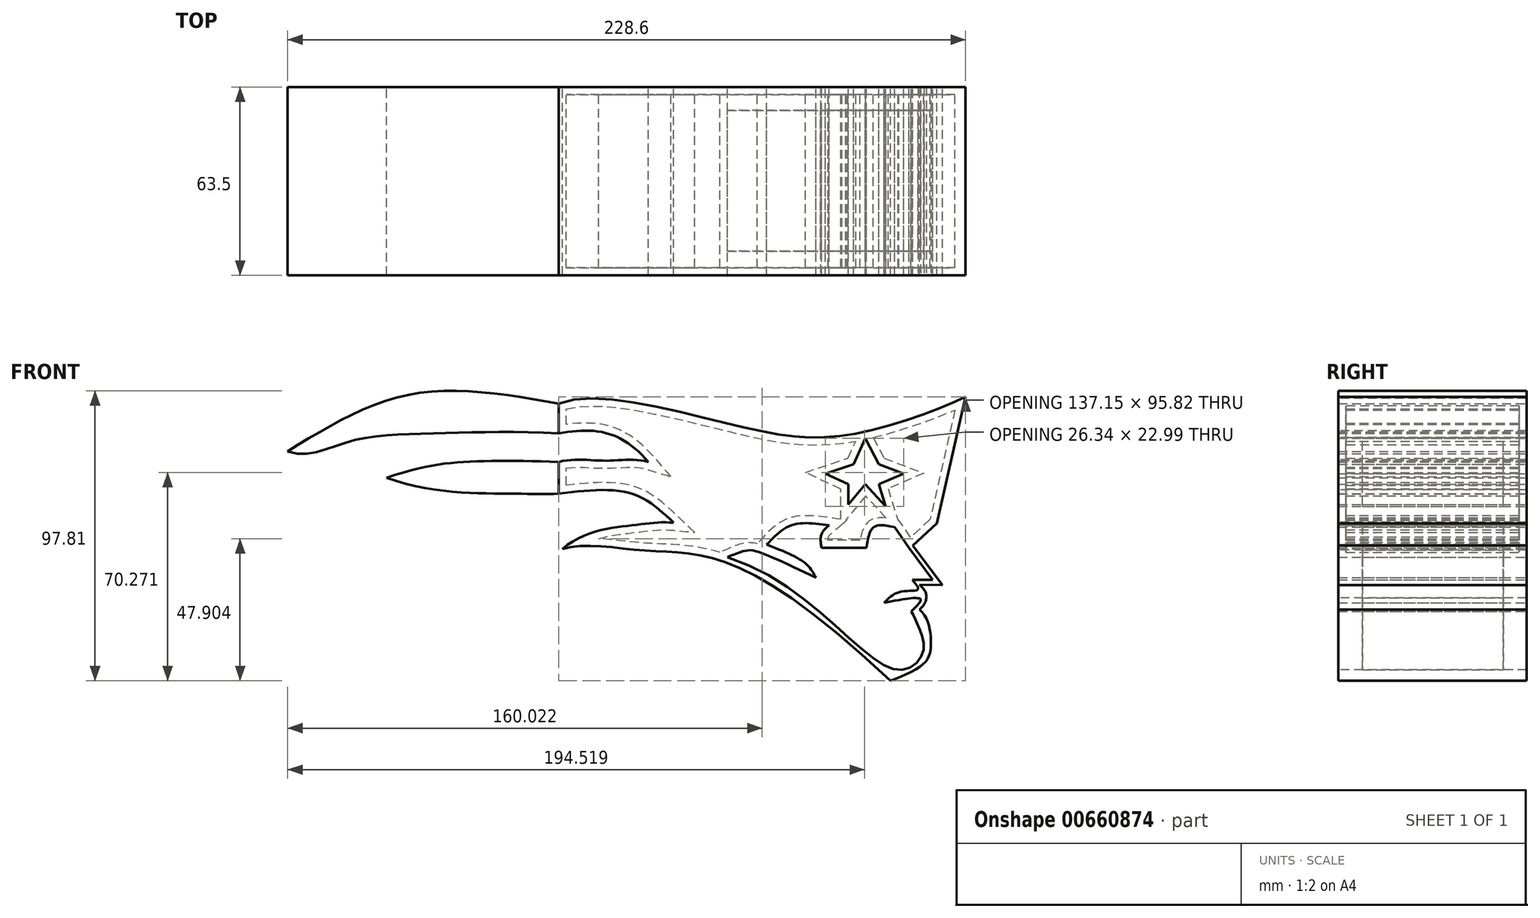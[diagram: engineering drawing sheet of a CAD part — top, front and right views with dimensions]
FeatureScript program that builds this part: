
annotation { "Feature Type Name" : "Feature", "Feature Type Description" : "" }
export const myFeature = defineFeature(function(context is Context, id is Id, definition is map)
    precondition{}
    {
        {
            var Q0;
            Q0=qCreatedBy(makeId("Front.planeOp"),FACE);
            var sketch = newSketch(context, id + "F0", { "sketchPlane" : qUnion([Q0])});
            skFitSpline(sketch, "E0", {"points": [v(-76.55, 30.41) * mm, v(-14.84, 22.52) * mm, v(22.56, 20.11) * mm, v(60.6, 32.7) * mm], "startDerivative": vector(105.9, 41.24) * mm, "endDerivative": vector(88.2, 42.73) * mm});
            skLineSegment(sketch, "E1", {"start": v(60.6, 32.7) * mm, "end": v(50.93, -9.95) * mm});
            skLineSegment(sketch, "E2", {"start": v(50.93, -9.95) * mm, "end": v(42.8, -17.48) * mm});
            skLineSegment(sketch, "E3", {"start": v(42.8, -17.48) * mm, "end": v(52.74, -30.8) * mm});
            skLineSegment(sketch, "E4", {"start": v(52.74, -30.8) * mm, "end": v(45.1, -30.75) * mm});
            skFitSpline(sketch, "E5", {"points": [v(45.1, -39.14) * mm, v(48.83, -51.49) * mm, v(35.22, -63.12) * mm], "startDerivative": vector(21.41, -17.74) * mm, "endDerivative": vector(-66.1, -25.1) * mm});
            skFitSpline(sketch, "E6", {"points": [v(35.22, -63.12) * mm, v(-46.74, -19.26) * mm, v(-75.4, -18.63) * mm], "startDerivative": vector(-230.88, 217.03) * mm, "endDerivative": vector(-62.71, -20.1) * mm});
            skFitSpline(sketch, "E7", {"points": [v(-75.4, -18.63) * mm, v(-51.4, -10.6) * mm, v(-37.88, -9.8) * mm], "startDerivative": vector(40.06, 33.3) * mm, "endDerivative": vector(31.5, -3.1) * mm});
            skFitSpline(sketch, "E8", {"points": [v(-37.88, -9.8) * mm, v(-51.92, 0) * mm, v(-76.55, 0) * mm], "startDerivative": vector(-27.63, 26.46) * mm, "endDerivative": vector(-49.07, -5.88) * mm});
            skLineSegment(sketch, "E9", {"start": v(-76.55, 0) * mm, "end": v(-76.55, 10.68) * mm});
            skFitSpline(sketch, "E10", {"points": [v(-76.55, 10.68) * mm, v(-60.93, 11.13) * mm, v(-46.36, 10.68) * mm], "startDerivative": vector(31.02, 8.7) * mm, "endDerivative": vector(29.37, -8.8) * mm});
            skFitSpline(sketch, "E11", {"points": [v(-46.36, 10.68) * mm, v(-60.4, 20.4) * mm, v(-76.55, 20.4) * mm], "startDerivative": vector(-25.48, 29.64) * mm, "endDerivative": vector(-35.03, -5.68) * mm});
            skLineSegment(sketch, "E12", {"start": v(-76.55, 20.4) * mm, "end": v(-76.55, 30.41) * mm});
            skFitSpline(sketch, "E13", {"points": [v(45.1, -30.75) * mm, v(47.36, -34.55) * mm, v(45.1, -39.14) * mm], "startDerivative": vector(9.64, -8.77) * mm, "endDerivative": vector(-9.59, -9.18) * mm});
            skLineSegment(sketch, "E14", {"start": v(22.81, 9.94) * mm, "end": v(26.74, 18.65) * mm});
            skLineSegment(sketch, "E15", {"start": v(26.74, 18.65) * mm, "end": v(31.35, 9.94) * mm});
            skLineSegment(sketch, "E16", {"start": v(31.35, 9.94) * mm, "end": v(39.69, 6.75) * mm});
            skLineSegment(sketch, "E17", {"start": v(39.69, 6.75) * mm, "end": v(31.35, 3.15) * mm});
            skLineSegment(sketch, "E18", {"start": v(31.35, 3.15) * mm, "end": v(33.67, -4.34) * mm});
            skLineSegment(sketch, "E19", {"start": v(33.67, -4.34) * mm, "end": v(26.74, 3.15) * mm});
            skLineSegment(sketch, "E20", {"start": v(26.74, 3.15) * mm, "end": v(21.08, -3.72) * mm});
            skLineSegment(sketch, "E21", {"start": v(21.08, -3.72) * mm, "end": v(21.08, 3.15) * mm});
            skLineSegment(sketch, "E22", {"start": v(21.08, 3.15) * mm, "end": v(13.35, 6.75) * mm});
            skLineSegment(sketch, "E23", {"start": v(13.35, 6.75) * mm, "end": v(22.81, 9.94) * mm});
            skFitSpline(sketch, "E24", {"points": [v(-19.72, -21.46) * mm, v(37.16, -59.31) * mm, v(46.35, -53) * mm, v(44.17, -43.7) * mm, v(42.26, -39.7) * mm], "startDerivative": vector(172.05, -53.12) * mm, "endDerivative": vector(-18.1, 19.47) * mm});
            skFitSpline(sketch, "E25", {"points": [v(42.26, -39.7) * mm, v(45.37, -35.66) * mm, v(33.17, -36.79) * mm], "startDerivative": vector(13.42, 12.7) * mm, "endDerivative": vector(-28.57, -5.56) * mm});
            skFitSpline(sketch, "E26", {"points": [v(33.17, -36.79) * mm, v(38.55, -33.1) * mm, v(44.46, -32.3) * mm, v(42.61, -29.06) * mm], "startDerivative": vector(12.2, 12.85) * mm, "endDerivative": vector(-12.3, 14.26) * mm});
            skLineSegment(sketch, "E27", {"start": v(42.61, -29.06) * mm, "end": v(49.56, -29.06) * mm});
            skLineSegment(sketch, "E28", {"start": v(49.56, -29.06) * mm, "end": v(41.46, -18.3) * mm});
            skLineSegment(sketch, "E29", {"start": v(41.46, -18.3) * mm, "end": v(36.6, -11.3) * mm});
            skFitSpline(sketch, "E30", {"points": [v(36.6, -11.3) * mm, v(29.63, -11.3) * mm, v(27.15, -18.3) * mm], "startDerivative": vector(-16.46, 3.4) * mm, "endDerivative": vector(-2.53, -17.3) * mm});
            skLineSegment(sketch, "E31", {"start": v(27.15, -18.3) * mm, "end": v(17.15, -18.3) * mm});
            skLineSegment(sketch, "E32", {"start": v(17.15, -18.3) * mm, "end": v(11.98, -18.3) * mm});
            skFitSpline(sketch, "E33", {"points": [v(11.98, -18.3) * mm, v(11.98, -13.65) * mm, v(14.56, -10.67) * mm], "startDerivative": vector(-1.4, 9.63) * mm, "endDerivative": vector(6.67, 5.57) * mm});
            skFitSpline(sketch, "E34", {"points": [v(14.56, -10.67) * mm, v(1.83, -10.67) * mm, v(-6.47, -17.19) * mm], "startDerivative": vector(-26.12, 3.58) * mm, "endDerivative": vector(-15.77, -16.93) * mm});
            skFitSpline(sketch, "E35", {"points": [v(-6.47, -17.19) * mm, v(6.53, -23.48) * mm, v(10.11, -28.33) * mm], "startDerivative": vector(25.14, -9.75) * mm, "endDerivative": vector(6.71, -12.76) * mm});
            skFitSpline(sketch, "E36", {"points": [v(10.11, -28.33) * mm, v(-8.13, -20.05) * mm, v(-13.26, -19.16) * mm, v(-19.72, -21.46) * mm], "startDerivative": vector(-44.29, 21.12) * mm, "endDerivative": vector(-24.53, -10.88) * mm});
            skPoint(sketch, "E37.2.internal.snap0", {"position": v(-76.55, 5.34) * mm});
            skFitSpline(sketch, "E37", {"points": [v(-76.55, 10.68) * mm, v(-108.96, 10.68) * mm, v(-134.69, 5.34) * mm], "startDerivative": vector(-72.18, 2.86) * mm, "endDerivative": vector(-71.3, -24.14) * mm});
            skFitSpline(sketch, "E38", {"points": [v(-134.69, 5.34) * mm, v(-93.5, 0) * mm, v(-76.55, 0) * mm], "startDerivative": vector(74.49, -26.26) * mm, "endDerivative": vector(38.7, 1.31) * mm});
            skFitSpline(sketch, "E39", {"points": [v(-76.55, 30.41) * mm, v(-126.5, 33.5) * mm, v(-168, 14.28) * mm], "startDerivative": vector(-100.97, 17.64) * mm, "endDerivative": vector(-81.78, -50.43) * mm});
            skFitSpline(sketch, "E40", {"points": [v(-168, 14.28) * mm, v(-146.96, 17.64) * mm, v(-119.9, 20.32) * mm, v(-76.55, 20.4) * mm], "startDerivative": vector(73.22, -27.17) * mm, "endDerivative": vector(121.44, -6.34) * mm});
            skSolve(sketch);
        }
        {
            var Q0;
            Q0=makeQuery(id+"F0.imprint","IMPRINT",FACE,{"disambiguationData":[TD([[makeQuery(id+"F0.imprint","IMPRINT",EDGE,{"derivedFrom":sQuery(id+"F0.wireOp",EDGE,"E0")}),-1.0]])]});
            extrude(context, id + "F1", {"entities" : qUnion([Q0]), "depth" : 63.5 * mm, "offsetDistance" : 25.4 * mm});
        }
        {
            var Q0;
            Q0=makeQuery(id+"F0.imprint","IMPRINT",FACE,{"disambiguationData":[TD([[makeQuery(id+"F0.imprint","IMPRINT",EDGE,{"derivedFrom":sQuery(id+"F0.wireOp",EDGE,"E12")}),1.0]])]});
            var Q1;
            Q1=makeQuery(id+"F0.imprint","IMPRINT",FACE,{"disambiguationData":[TD([[makeQuery(id+"F0.imprint","IMPRINT",EDGE,{"derivedFrom":sQuery(id+"F0.wireOp",EDGE,"E9")}),1.0]])]});
            extrude(context, id + "F2", {"entities" : qUnion([Q0, Q1]), "depth" : 63.5 * mm, "offsetDistance" : 25.4 * mm});
        }
        {
            var Q0;
            Q0=makeQuery(id+"F0.imprint","IMPRINT",FACE,{"disambiguationData":[TD([[makeQuery(id+"F0.imprint","IMPRINT",EDGE,{"derivedFrom":sQuery(id+"F0.wireOp",EDGE,"E24")}),1.0]])]});
            var Q1;
            Q1=makeQuery(id+"F0.imprint","IMPRINT",FACE,{"disambiguationData":[TD([[makeQuery(id+"F0.imprint","IMPRINT",EDGE,{"derivedFrom":sQuery(id+"F0.wireOp",EDGE,"E14")}),-1.0]])]});
            extrude(context, id + "F3", {"entities" : qUnion([Q0, Q1]), "depth" : 55.37 * mm, "offsetDistance" : 25.4 * mm, "hasSecondDirection" : true, "secondDirectionOppositeDirection" : false, "secondDirectionDepth" : 7.82 * mm});
        }
        {
            var Q0;
            Q0=makeQuery(id+"F1.opExtrude","CAP_FACE",FACE,{"disambiguationData":[OSD([sQuery(id+"F0.wireOp",EDGE,"E0"),sQuery(id+"F0.wireOp",EDGE,"E1"),sQuery(id+"F0.wireOp",EDGE,"E2"),sQuery(id+"F0.wireOp",EDGE,"E3"),sQuery(id+"F0.wireOp",EDGE,"E4"),sQuery(id+"F0.wireOp",EDGE,"E5"),sQuery(id+"F0.wireOp",EDGE,"E6"),sQuery(id+"F0.wireOp",EDGE,"E7"),sQuery(id+"F0.wireOp",EDGE,"E8"),sQuery(id+"F0.wireOp",EDGE,"E9"),sQuery(id+"F0.wireOp",EDGE,"E10"),sQuery(id+"F0.wireOp",EDGE,"E11"),sQuery(id+"F0.wireOp",EDGE,"E12"),sQuery(id+"F0.wireOp",EDGE,"E13"),sQuery(id+"F0.wireOp",EDGE,"E14"),sQuery(id+"F0.wireOp",EDGE,"E15"),sQuery(id+"F0.wireOp",EDGE,"E16"),sQuery(id+"F0.wireOp",EDGE,"E17"),sQuery(id+"F0.wireOp",EDGE,"E18"),sQuery(id+"F0.wireOp",EDGE,"E19"),sQuery(id+"F0.wireOp",EDGE,"E20"),sQuery(id+"F0.wireOp",EDGE,"E21"),sQuery(id+"F0.wireOp",EDGE,"E22"),sQuery(id+"F0.wireOp",EDGE,"E23"),sQuery(id+"F0.wireOp",EDGE,"E24"),sQuery(id+"F0.wireOp",EDGE,"E25"),sQuery(id+"F0.wireOp",EDGE,"E26"),sQuery(id+"F0.wireOp",EDGE,"E27"),sQuery(id+"F0.wireOp",EDGE,"E28"),sQuery(id+"F0.wireOp",EDGE,"E29"),sQuery(id+"F0.wireOp",EDGE,"E30"),sQuery(id+"F0.wireOp",EDGE,"E31"),sQuery(id+"F0.wireOp",EDGE,"E32"),sQuery(id+"F0.wireOp",EDGE,"E33"),sQuery(id+"F0.wireOp",EDGE,"E34"),sQuery(id+"F0.wireOp",EDGE,"E35"),sQuery(id+"F0.wireOp",EDGE,"E36")])],"isStart":false});
            var Q1;
            Q1=makeQuery(id+"F1.opExtrude","SWEPT_BODY",BODY,{"disambiguationData":[OSD([sQuery(id+"F0.wireOp",EDGE,"E0"),sQuery(id+"F0.wireOp",EDGE,"E1"),sQuery(id+"F0.wireOp",EDGE,"E2"),sQuery(id+"F0.wireOp",EDGE,"E3"),sQuery(id+"F0.wireOp",EDGE,"E4"),sQuery(id+"F0.wireOp",EDGE,"E5"),sQuery(id+"F0.wireOp",EDGE,"E6"),sQuery(id+"F0.wireOp",EDGE,"E7"),sQuery(id+"F0.wireOp",EDGE,"E8"),sQuery(id+"F0.wireOp",EDGE,"E9"),sQuery(id+"F0.wireOp",EDGE,"E10"),sQuery(id+"F0.wireOp",EDGE,"E11"),sQuery(id+"F0.wireOp",EDGE,"E12"),sQuery(id+"F0.wireOp",EDGE,"E13"),sQuery(id+"F0.wireOp",EDGE,"E14"),sQuery(id+"F0.wireOp",EDGE,"E15"),sQuery(id+"F0.wireOp",EDGE,"E16"),sQuery(id+"F0.wireOp",EDGE,"E17"),sQuery(id+"F0.wireOp",EDGE,"E18"),sQuery(id+"F0.wireOp",EDGE,"E19"),sQuery(id+"F0.wireOp",EDGE,"E20"),sQuery(id+"F0.wireOp",EDGE,"E21"),sQuery(id+"F0.wireOp",EDGE,"E22"),sQuery(id+"F0.wireOp",EDGE,"E23"),sQuery(id+"F0.wireOp",EDGE,"E24"),sQuery(id+"F0.wireOp",EDGE,"E25"),sQuery(id+"F0.wireOp",EDGE,"E26"),sQuery(id+"F0.wireOp",EDGE,"E27"),sQuery(id+"F0.wireOp",EDGE,"E28"),sQuery(id+"F0.wireOp",EDGE,"E29"),sQuery(id+"F0.wireOp",EDGE,"E30"),sQuery(id+"F0.wireOp",EDGE,"E31"),sQuery(id+"F0.wireOp",EDGE,"E32"),sQuery(id+"F0.wireOp",EDGE,"E33"),sQuery(id+"F0.wireOp",EDGE,"E34"),sQuery(id+"F0.wireOp",EDGE,"E35"),sQuery(id+"F0.wireOp",EDGE,"E36")])]});
            shell(context, id + "F4", {"isHollow" : true, "entities" : qUnion([Q0]), "parts" : qUnion([Q1]), "thickness" : 2.54 * mm});
        }
    });
